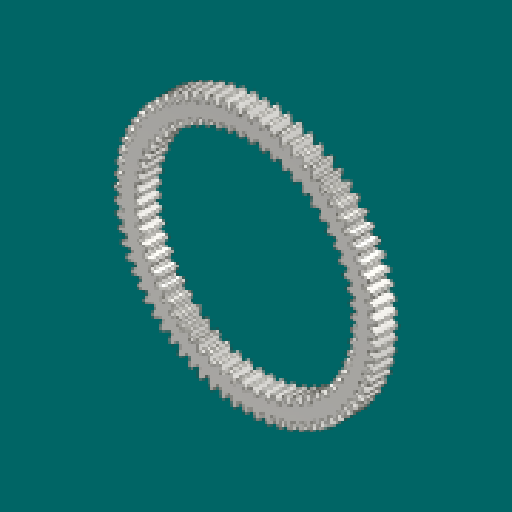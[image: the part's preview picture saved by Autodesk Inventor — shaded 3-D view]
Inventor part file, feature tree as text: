
AUTODESK INVENTOR PART (.ipt)
format: ipt  version: 2023.1 (Build 271208000, 208)  size: 806,912 bytes
history: native  units: mm (DEFAULTED — no unit token found)
features: other x6, plane x3, sketch x3, extrude x2, boolean_combine x1
ambient origin geometry x8: Origin, YZ Plane, XZ Plane, XY Plane, X Axis, Y Axis, Z Axis, Center Point
bodies: Solid1 (feature_tree), Solid1_1 (feature_tree)
feature tree (15):
  other  "Spur Gear2"
  extrude  "Extrusion1"  Depth=7.62mm TaperAngle=0.0deg
  plane  "Work Plane1"
  plane  "Work Plane2"
  plane  "Work Plane3"
  other  "Spur Gear"
  extrude  "Extrusion2"  Depth=76.2mm TaperAngle=0.0deg
  boolean_combine  "Combine1"
  sketch  "Sketch1"  dims[d0=93.98mm d1=7.62mm d2=0.0mm]
  sketch  "Sketch2"  dims[d3=91.44mm d4=76.2mm d5=0.0mm]
  other  "Srf1"
  sketch  "Sketch3"  dims[d6=0.0mm d7=0.436332mm d9=0.0mm d14=0.0mm d15=91.44mm d16=0.0mm d17=0.0mm d18=0.0mm d19=91.44mm d20=83.82mm d21=0.0mm d22=0.0mm d23=10.0mm]
  other  "Solid1::Spur Gear2"
  other  "TaggingFeature1"
  other  "Pitch Diameter"
